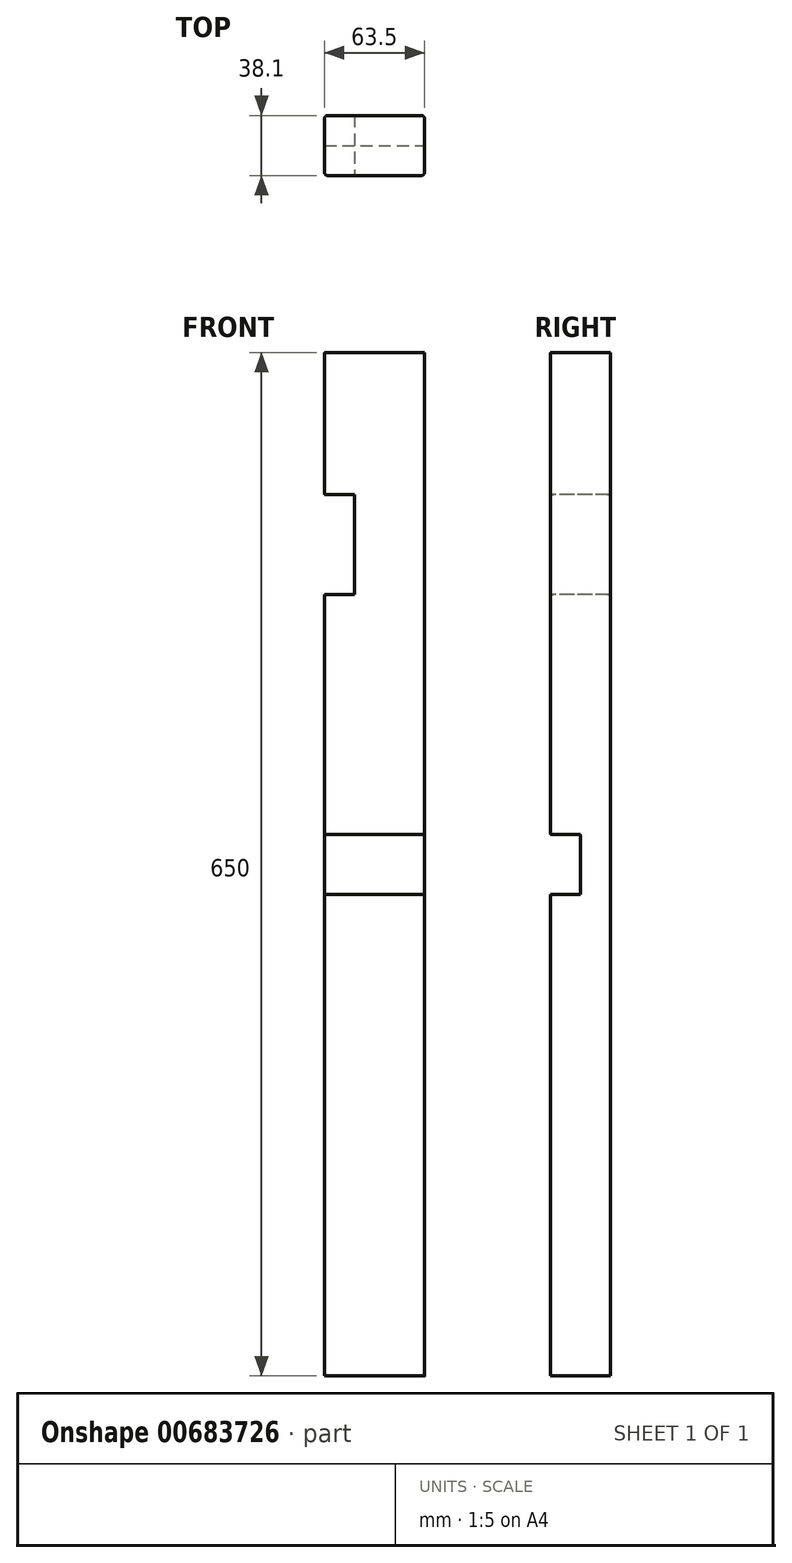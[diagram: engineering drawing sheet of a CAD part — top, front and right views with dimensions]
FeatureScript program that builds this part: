
annotation { "Feature Type Name" : "Feature", "Feature Type Description" : "" }
export const myFeature = defineFeature(function(context is Context, id is Id, definition is map)
    precondition{}
    {
        {
            var Q0;
            Q0=qCreatedBy(makeId("Top.planeOp"),FACE);
            var sketch = newSketch(context, id + "F0", { "sketchPlane" : qUnion([Q0])});
            skLineSegment(sketch, "E0.bottom", {"start": v(-31.75, 19.05) * mm, "end": v(31.75, 19.05) * mm});
            skLineSegment(sketch, "E0.top", {"start": v(-31.75, -19.05) * mm, "end": v(31.75, -19.05) * mm});
            skLineSegment(sketch, "E0.left", {"start": v(-31.75, 19.05) * mm, "end": v(-31.75, -19.05) * mm});
            skLineSegment(sketch, "E0.right", {"start": v(31.75, 19.05) * mm, "end": v(31.75, -19.05) * mm});
            skSolve(sketch);
        }
        {
            var Q0;
            Q0=qSketchRegion(id+"F0",true);
            extrude(context, id + "F1", {"entities" : qUnion([Q0]), "depth" : 650 * mm, "offsetDistance" : 25 * mm});
        }
        {
            var Q0;
            Q0=makeQuery(id+"F1.opExtrude","SWEPT_EDGE",EDGE,{"disambiguationData":[OSD([sQuery(id+"F0.wireOp",EDGE,"E0.top"),sQuery(id+"F0.wireOp",EDGE,"E0.left")])]});
            var Q1;
            Q1=makeQuery(id+"F1.opExtrude","SWEPT_EDGE",EDGE,{"disambiguationData":[OSD([sQuery(id+"F0.wireOp",EDGE,"E0.top"),sQuery(id+"F0.wireOp",EDGE,"E0.right")])]});
            var Q2;
            Q2=makeQuery(id+"F1.opExtrude","SWEPT_EDGE",EDGE,{"disambiguationData":[OSD([sQuery(id+"F0.wireOp",EDGE,"E0.bottom"),sQuery(id+"F0.wireOp",EDGE,"E0.right")])]});
            var Q3;
            Q3=makeQuery(id+"F1.opExtrude","SWEPT_EDGE",EDGE,{"disambiguationData":[OSD([sQuery(id+"F0.wireOp",EDGE,"E0.bottom"),sQuery(id+"F0.wireOp",EDGE,"E0.left")])]});
            fillet(context, id + "F2", {"entities" : qUnion([Q0, Q1, Q2, Q3]), "radius" : 2 * mm, "tangentPropagation" : true, "allowEdgeOverflow" : false});
        }
        {
            var Q0;
            Q0=makeQuery(id+"F1.opExtrude","SWEPT_FACE",FACE,{"disambiguationData":[OSD([sQuery(id+"F0.wireOp",EDGE,"E0.top")])]});
            var sketch = newSketch(context, id + "F3", { "sketchPlane" : qUnion([Q0])});
            skLineSegment(sketch, "E1", {"start": v(0, 650) * mm, "end": v(0, 0) * mm});
            skLineSegment(sketch, "E2", {"start": v(-71.1, 325) * mm, "end": v(101.97, 325) * mm});
            skPoint(sketch, "E3.orphan", {"position": v(0, 325) * mm});
            skLineSegment(sketch, "E4.0", {"start": v(-71.1, 305.95) * mm, "end": v(101.97, 305.95) * mm});
            skLineSegment(sketch, "E5.0", {"start": v(-71.1, 344.05) * mm, "end": v(101.97, 344.05) * mm});
            skLineSegment(sketch, "E6", {"start": v(-44.1, 376.34) * mm, "end": v(-44.1, 277.04) * mm});
            skLineSegment(sketch, "E7", {"start": v(48.94, 379.23) * mm, "end": v(48.94, 272.21) * mm});
            skSolve(sketch);
        }
        {
            var Q0;
            Q0=qSketchRegion(id+"F3",true);
            extrude(context, id + "F4", {"entities" : qUnion([Q0]), "operationType" : NewBodyOperationType.REMOVE, "oppositeDirection" : true, "depth" : 19.05 * mm, "offsetDistance" : 25 * mm});
        }
        {
            var Q0;
            Q0=makeQuery(id+"F1.opExtrude","SWEPT_FACE",FACE,{"disambiguationData":[OSD([sQuery(id+"F0.wireOp",EDGE,"E0.left")])]});
            var sketch = newSketch(context, id + "F5", { "sketchPlane" : qUnion([Q0])});
            skLineSegment(sketch, "E8.0", {"start": v(-64.92, 496.25) * mm, "end": v(31.26, 496.25) * mm});
            skLineSegment(sketch, "E9.0", {"start": v(-64.92, 560) * mm, "end": v(31.26, 560) * mm});
            skLineSegment(sketch, "E10", {"start": v(31.26, 560) * mm, "end": v(31.26, 496.25) * mm});
            skLineSegment(sketch, "E11", {"start": v(-64.92, 560) * mm, "end": v(-64.92, 496.25) * mm});
            skSolve(sketch);
        }
        {
            var Q0;
            Q0=qSketchRegion(id+"F5",true);
            extrude(context, id + "F6", {"entities" : qUnion([Q0]), "operationType" : NewBodyOperationType.REMOVE, "oppositeDirection" : true, "depth" : 19.05 * mm, "offsetDistance" : 25 * mm});
        }
    });
